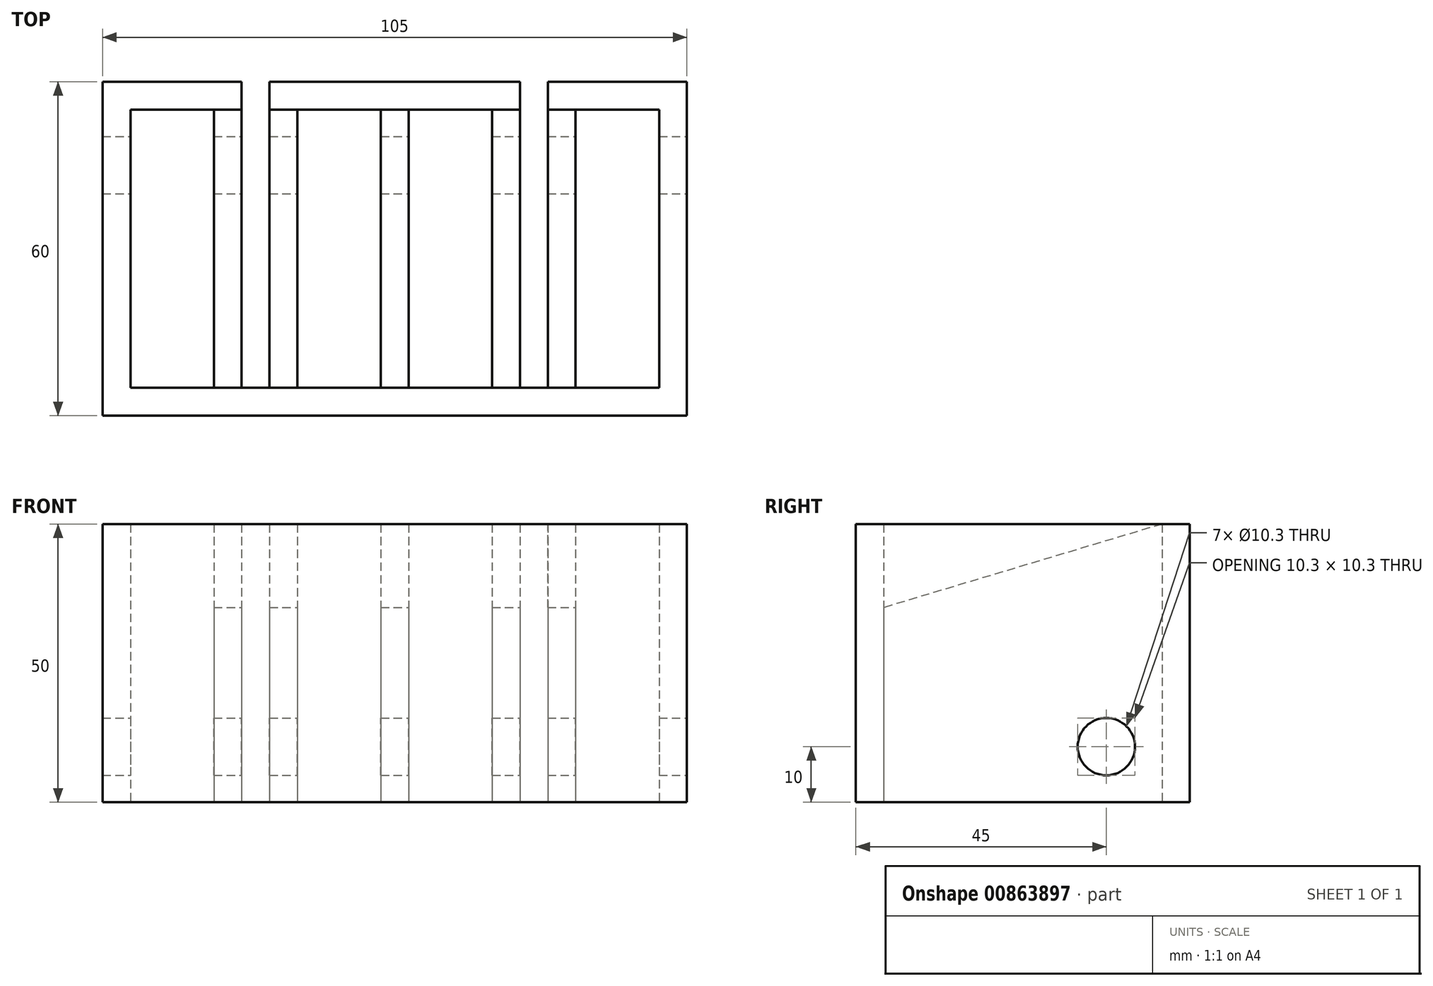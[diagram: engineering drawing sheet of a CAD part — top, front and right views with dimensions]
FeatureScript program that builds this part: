
annotation { "Feature Type Name" : "Feature", "Feature Type Description" : "" }
export const myFeature = defineFeature(function(context is Context, id is Id, definition is map)
    precondition{}
    {
        {
            var Q0;
            Q0=qCreatedBy(makeId("Top.planeOp"),FACE);
            var sketch = newSketch(context, id + "F0", { "sketchPlane" : qUnion([Q0])});
            skLineSegment(sketch, "E0.bottom", {"start": v(47.5, -25) * mm, "end": v(32.5, -25) * mm});
            skLineSegment(sketch, "E0.top", {"start": v(47.5, 25) * mm, "end": v(32.5, 25) * mm});
            skLineSegment(sketch, "E0.left", {"start": v(47.5, -25) * mm, "end": v(47.5, 25) * mm});
            skLineSegment(sketch, "E0.right", {"start": v(-47.5, -25) * mm, "end": v(-47.5, 25) * mm});
            skPoint(sketch, "E0.middle", {"position": v(0, 0) * mm});
            skLineSegment(sketch, "E1.0", {"start": v(52.5, 30) * mm, "end": v(27.5, 30) * mm});
            skLineSegment(sketch, "E1.1", {"start": v(52.5, -30) * mm, "end": v(52.5, 30) * mm});
            skLineSegment(sketch, "E1.2", {"start": v(52.5, -30) * mm, "end": v(-52.5, -30) * mm});
            skLineSegment(sketch, "E1.3", {"start": v(-52.5, -30) * mm, "end": v(-52.5, 30) * mm});
            skLineSegment(sketch, "E2.left", {"start": v(-32.5, 25) * mm, "end": v(-32.5, -25) * mm});
            skLineSegment(sketch, "E2.right", {"start": v(-27.5, 25) * mm, "end": v(-27.5, -25) * mm});
            skLineSegment(sketch, "E3.left", {"start": v(-22.5, 25) * mm, "end": v(-22.5, -25) * mm});
            skLineSegment(sketch, "E3.right", {"start": v(-17.5, 25) * mm, "end": v(-17.5, -25) * mm});
            skLineSegment(sketch, "E4.left", {"start": v(-2.5, 25) * mm, "end": v(-2.5, -25) * mm});
            skLineSegment(sketch, "E4.right", {"start": v(2.5, 25) * mm, "end": v(2.5, -25) * mm});
            skLineSegment(sketch, "E5.left", {"start": v(17.5, 25) * mm, "end": v(17.5, -25) * mm});
            skLineSegment(sketch, "E5.right", {"start": v(22.5, 25) * mm, "end": v(22.5, -25) * mm});
            skLineSegment(sketch, "E6.left", {"start": v(27.5, 25) * mm, "end": v(27.5, -25) * mm});
            skLineSegment(sketch, "E6.right", {"start": v(32.5, 25) * mm, "end": v(32.5, -25) * mm});
            skLineSegment(sketch, "E7.trimOffspring", {"start": v(-32.5, 25) * mm, "end": v(-47.5, 25) * mm});
            skLineSegment(sketch, "E8.trimOffspring", {"start": v(-32.5, -25) * mm, "end": v(-47.5, -25) * mm});
            skLineSegment(sketch, "E9.trimOffspring", {"start": v(-22.5, -25) * mm, "end": v(-27.5, -25) * mm});
            skLineSegment(sketch, "E10.trimOffspring", {"start": v(-2.5, 25) * mm, "end": v(-17.5, 25) * mm});
            skLineSegment(sketch, "E11.trimOffspring", {"start": v(-2.5, -25) * mm, "end": v(-17.5, -25) * mm});
            skLineSegment(sketch, "E12.trimOffspring", {"start": v(17.5, -25) * mm, "end": v(2.5, -25) * mm});
            skLineSegment(sketch, "E13.trimOffspring", {"start": v(17.5, 25) * mm, "end": v(2.5, 25) * mm});
            skLineSegment(sketch, "E14.trimOffspring", {"start": v(27.5, -25) * mm, "end": v(22.5, -25) * mm});
            skLineSegment(sketch, "E15", {"start": v(27.5, 25) * mm, "end": v(27.5, 30) * mm});
            skLineSegment(sketch, "E16", {"start": v(22.5, 25) * mm, "end": v(22.5, 30) * mm});
            skLineSegment(sketch, "E17.trimOffspring", {"start": v(22.5, 30) * mm, "end": v(-22.5, 30) * mm});
            skLineSegment(sketch, "E18", {"start": v(-27.5, 25) * mm, "end": v(-27.5, 30) * mm});
            skLineSegment(sketch, "E19", {"start": v(-22.5, 30) * mm, "end": v(-22.5, 25) * mm});
            skLineSegment(sketch, "E20.trimOffspring", {"start": v(-27.5, 30) * mm, "end": v(-52.5, 30) * mm});
            skSolve(sketch);
        }
        {
            var Q0;
            Q0 = qSketchRegion(id + "F0", true);
            extrude(context, id + "F1", {"entities" : qUnion([Q0]), "depth" : 50 * mm, "offsetDistance" : 25 * mm});
        }
        {
            var Q0;
            Q0=makeQuery(id+"F1.opExtrude","SWEPT_FACE",FACE,{"disambiguationData":[OSD([sQuery(id+"F0.wireOp",EDGE,"E1.1")])]});
            var sketch = newSketch(context, id + "F2", { "sketchPlane" : qUnion([Q0])});
            skCircle(sketch, "E21", {"center": v(15, 10) * mm, "radius": 5.15 * mm});
            skSolve(sketch);
        }
        {
            var Q0;
            Q0 = qSketchRegion(id + "F2", true);
            extrude(context, id + "F3", {"entities" : qUnion([Q0]), "operationType" : NewBodyOperationType.REMOVE, "endBound" : BoundingType.THROUGH_ALL, "oppositeDirection" : true, "depth" : 25 * mm, "offsetDistance" : 25 * mm});
        }
        {
            var Q0;
            Q0=makeQuery(id+"F1.opExtrude","SWEPT_FACE",FACE,{"disambiguationData":[OSD([sQuery(id+"F0.wireOp",EDGE,"E6.right")])]});
            var sketch = newSketch(context, id + "F4", { "sketchPlane" : qUnion([Q0])});
            skLineSegment(sketch, "E22", {"start": v(25, 50) * mm, "end": v(-25, 35) * mm});
            skLineSegment(sketch, "E23", {"start": v(-25, 35) * mm, "end": v(-25, 50) * mm});
            skLineSegment(sketch, "E24", {"start": v(-25, 50) * mm, "end": v(25, 50) * mm});
            skSolve(sketch);
        }
        {
            var Q0;
            Q0 = qSketchRegion(id + "F4", true);
            extrude(context, id + "F5", {"entities" : qUnion([Q0]), "operationType" : NewBodyOperationType.REMOVE, "oppositeDirection" : true, "depth" : 75 * mm, "offsetDistance" : 25 * mm});
        }
    });
